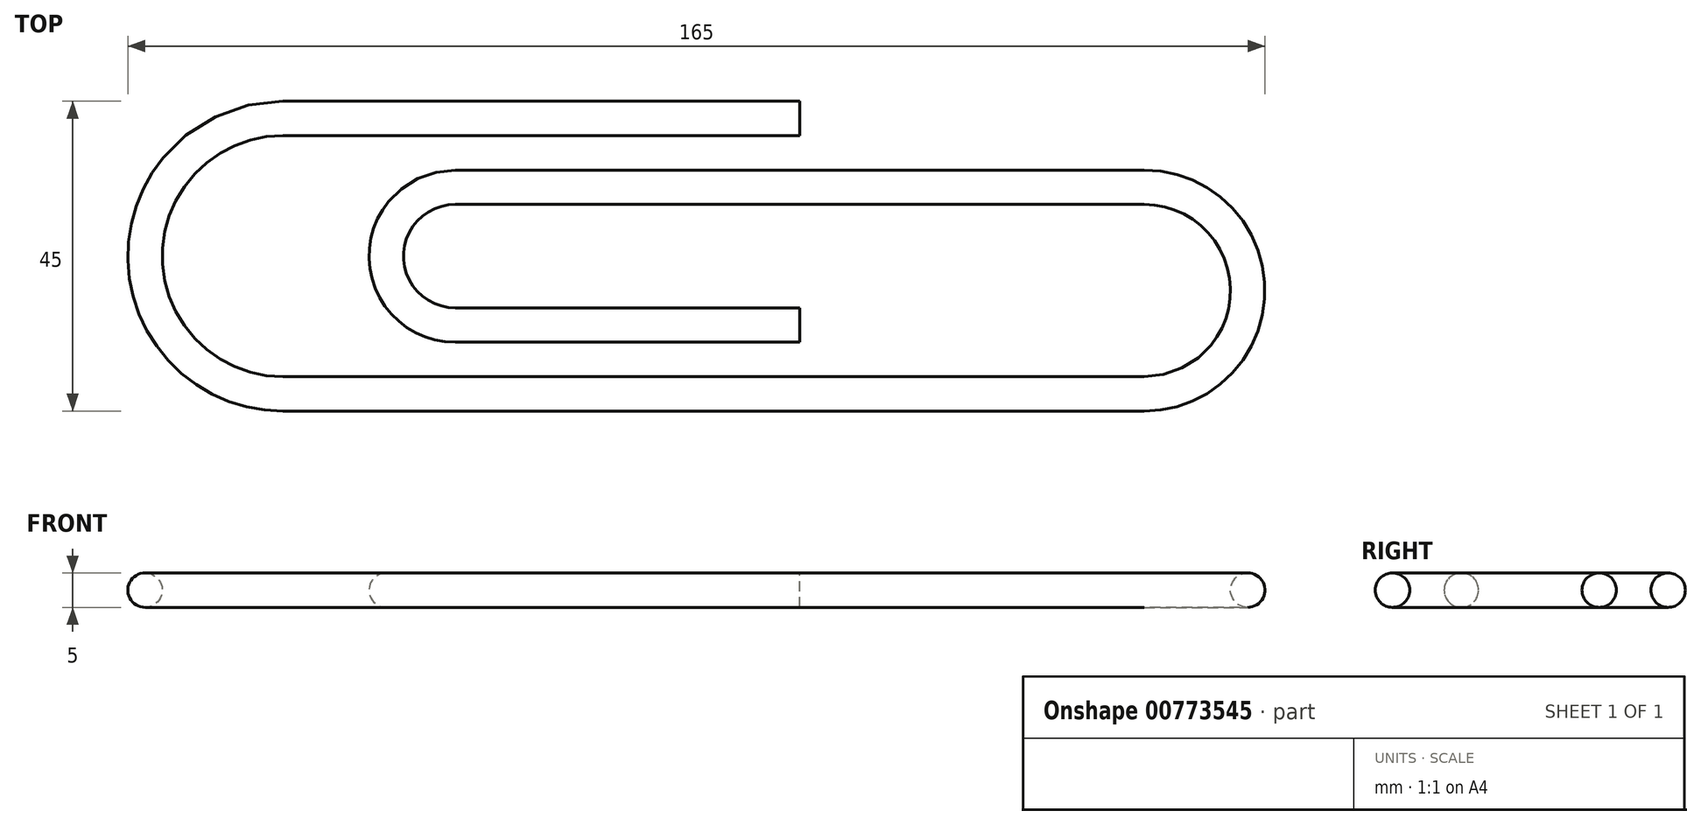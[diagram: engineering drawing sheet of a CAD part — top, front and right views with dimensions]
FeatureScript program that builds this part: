
annotation { "Feature Type Name" : "Feature", "Feature Type Description" : "" }
export const myFeature = defineFeature(function(context is Context, id is Id, definition is map)
    precondition{}
    {
        {
            var Q0;
            Q0=qCreatedBy(makeId("Top.planeOp"),FACE);
            var sketch = newSketch(context, id + "F0", { "sketchPlane" : qUnion([Q0])});
            skLineSegment(sketch, "E0", {"start": v(0, 0) * mm, "end": v(-75, 0) * mm});
            skLineSegment(sketch, "E1", {"start": v(-75, -40) * mm, "end": v(50, -40) * mm});
            skLineSegment(sketch, "E2", {"start": v(50, -10) * mm, "end": v(-50, -10) * mm});
            skLineSegment(sketch, "E3", {"start": v(-50, -30) * mm, "end": v(0, -30) * mm});
            skArc(sketch, "E4", {"start": v(-75, 0) * mm, "mid": v(-95, -20) * mm, "end": v(-75, -40) * mm});
            skArc(sketch, "E5", {"start": v(-50, -10) * mm, "mid": v(-60, -20) * mm, "end": v(-50, -30) * mm});
            skArc(sketch, "E6", {"start": v(50, -10) * mm, "mid": v(65, -25) * mm, "end": v(50, -40) * mm});
            skSolve(sketch);
        }
        {
            var Q0;
            Q0=qCreatedBy(makeId("Right.planeOp"),FACE);
            var sketch = newSketch(context, id + "F1", { "sketchPlane" : qUnion([Q0])});
            skCircle(sketch, "E7", {"center": v(0, 0) * mm, "radius": 2.5 * mm});
            skSolve(sketch);
        }
        {
            var Q0;
            Q0=qSketchRegion(id+"F1",true);
            var Q1;
            Q1=qConstructionFilter(qBodyType(qCreatedBy(id+"F0",EDGE),BodyType.WIRE),ConstructionObject.NO);
            sweep(context, id + "F2", {"profiles" : qUnion([Q0]), "path" : qUnion([Q1])});
        }
    });
